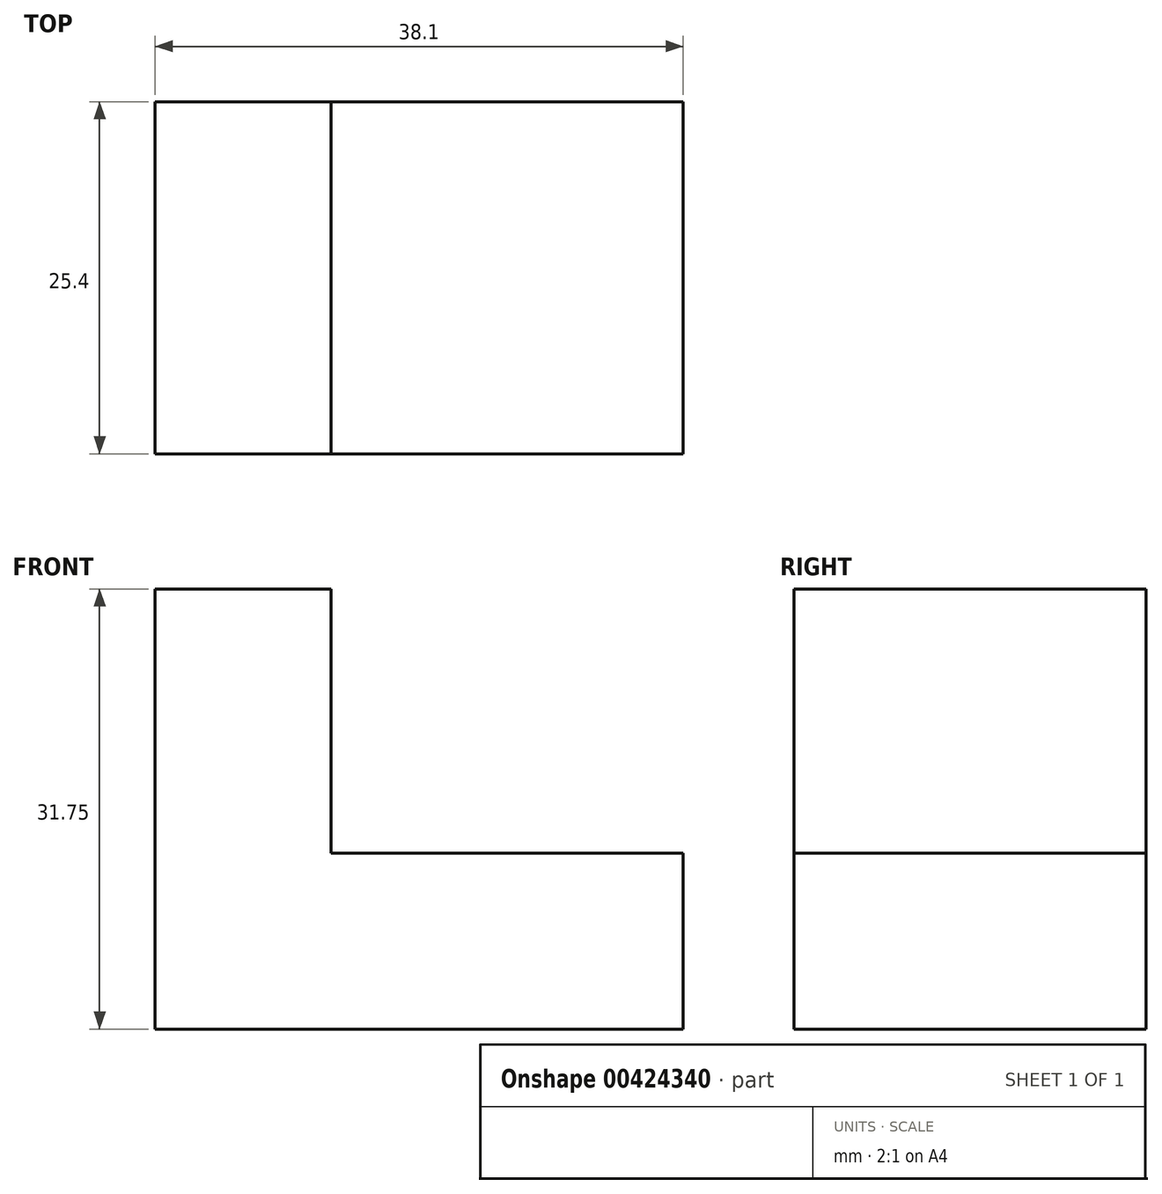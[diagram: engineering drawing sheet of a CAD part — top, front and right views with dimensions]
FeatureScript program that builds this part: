
annotation { "Feature Type Name" : "Feature", "Feature Type Description" : "" }
export const myFeature = defineFeature(function(context is Context, id is Id, definition is map)
    precondition{}
    {
        {
            var Q0;
            Q0=qCreatedBy(makeId("Front.planeOp"),FACE);
            var sketch = newSketch(context, id + "F0", { "sketchPlane" : qUnion([Q0])});
            skLineSegment(sketch, "E0", {"start": v(0, 0) * mm, "end": v(0, 31.75) * mm});
            skLineSegment(sketch, "E1", {"start": v(0, 31.75) * mm, "end": v(12.7, 31.75) * mm});
            skLineSegment(sketch, "E2", {"start": v(12.7, 31.75) * mm, "end": v(12.7, 12.7) * mm});
            skLineSegment(sketch, "E3", {"start": v(12.7, 12.7) * mm, "end": v(38.1, 12.7) * mm});
            skLineSegment(sketch, "E4", {"start": v(38.1, 12.7) * mm, "end": v(38.1, 0) * mm});
            skLineSegment(sketch, "E5", {"start": v(0, 0) * mm, "end": v(38.1, 0) * mm});
            skSolve(sketch);
        }
        {
            var Q0;
            Q0=makeQuery(id+"F0.imprint","IMPRINT",FACE,{"disambiguationData":[TD([[makeQuery(id+"F0.imprint","IMPRINT",EDGE,{"derivedFrom":sQuery(id+"F0.wireOp",EDGE,"E0")}),-1.0]])]});
            extrude(context, id + "F1", {"entities" : qUnion([Q0]), "depth" : 25.4 * mm});
        }
    });
